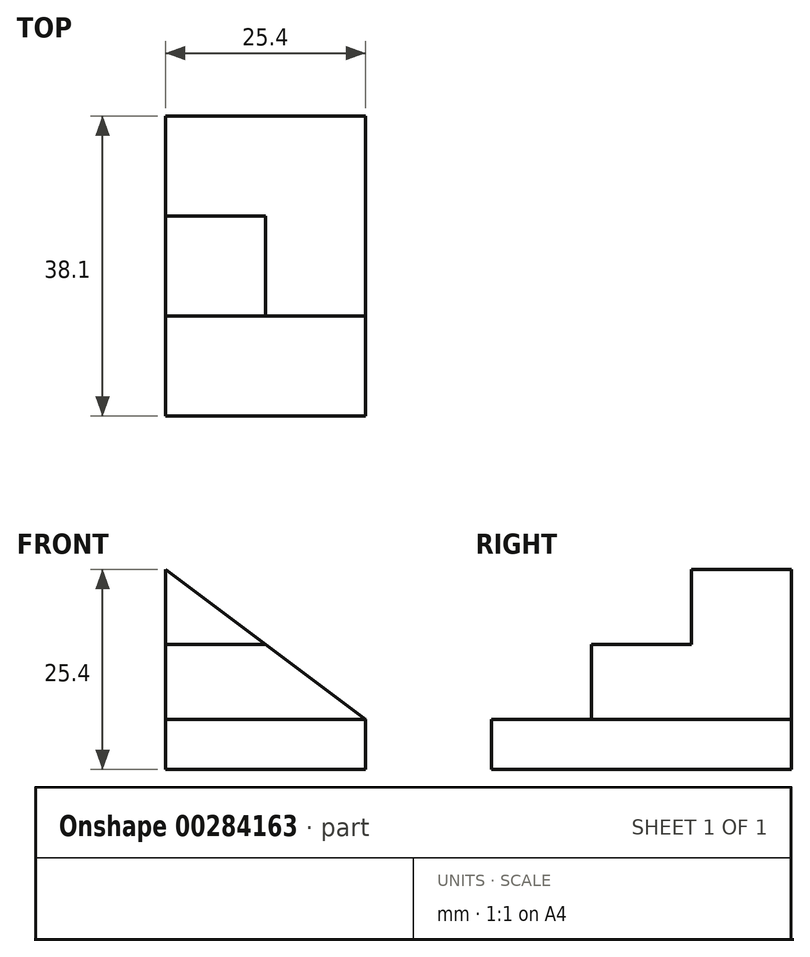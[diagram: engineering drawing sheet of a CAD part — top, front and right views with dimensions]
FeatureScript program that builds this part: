
annotation { "Feature Type Name" : "Feature", "Feature Type Description" : "" }
export const myFeature = defineFeature(function(context is Context, id is Id, definition is map)
    precondition{}
    {
        {
            var Q0;
            Q0=qCreatedBy(makeId("Front.planeOp"),FACE);
            var sketch = newSketch(context, id + "F0", { "sketchPlane" : qUnion([Q0])});
            skLineSegment(sketch, "E0.bottom", {"start": v(0, 0) * mm, "end": v(25.4, 0) * mm});
            skLineSegment(sketch, "E0.top", {"start": v(0, 6.35) * mm, "end": v(25.4, 6.35) * mm});
            skLineSegment(sketch, "E0.left", {"start": v(0, 0) * mm, "end": v(0, 6.35) * mm});
            skLineSegment(sketch, "E0.right", {"start": v(25.4, 0) * mm, "end": v(25.4, 6.35) * mm});
            skLineSegment(sketch, "E1.left", {"start": v(0, 6.35) * mm, "end": v(0, 19.05) * mm});
            skLineSegment(sketch, "E1.right", {"start": v(19.05, 6.35) * mm, "end": v(19.05, 11.11) * mm});
            skLineSegment(sketch, "E2.left", {"start": v(0, 19.05) * mm, "end": v(0, 25.4) * mm});
            skLineSegment(sketch, "E3", {"start": v(0, 25.4) * mm, "end": v(25.4, 6.35) * mm});
            skLineSegment(sketch, "E4", {"start": v(0, 19.05) * mm, "end": v(8.47, 19.05) * mm});
            skSolve(sketch);
        }
        {
            var Q0;
            Q0 = qSketchRegion(id + "F0", true);
            extrude(context, id + "F1", {"entities" : qUnion([Q0]), "depth" : 38.1 * mm});
        }
        {
            var Q0;
            Q0=makeQuery(id+"F1.opExtrude","CAP_FACE",FACE,{"disambiguationData":[OSD([sQuery(id+"F0.wireOp",EDGE,"E0.bottom"),sQuery(id+"F0.wireOp",EDGE,"E0.left"),sQuery(id+"F0.wireOp",EDGE,"E0.right"),sQuery(id+"F0.wireOp",EDGE,"E1.left"),sQuery(id+"F0.wireOp",EDGE,"E2.left"),sQuery(id+"F0.wireOp",EDGE,"E3")])],"isStart":false});
            var sketch = newSketch(context, id + "F2", { "sketchPlane" : qUnion([Q0])});
            skLineSegment(sketch, "E5", {"start": v(25.4, 6.35) * mm, "end": v(0, 6.35) * mm});
            skSolve(sketch);
        }
        {
            var Q0;
            {var subQ0=sQuery(id+"F2.wireOp",EDGE,"E5");Q0=makeQuery(id+"F2.imprint","IMPRINT",FACE,{"disambiguationData":[TD([[makeQuery(id+"F2.imprint","IMPRINT",EDGE,{"derivedFrom":subQ0}),-1.0]])]});}
            extrude(context, id + "F3", {"entities" : qUnion([Q0]), "operationType" : NewBodyOperationType.REMOVE, "oppositeDirection" : true, "depth" : 12.7 * mm});
        }
        {
            var Q0;
            Q0=makeQuery(id+"F3.boolean.opBoolean","COPY",FACE,{"derivedFrom":makeQuery(id+"F3.opExtrude","CAP_FACE",FACE,{"disambiguationData":[OSD([sQuery(id+"F0.wireOp",EDGE,"E0.left"),sQuery(id+"F0.wireOp",EDGE,"E1.left"),sQuery(id+"F0.wireOp",EDGE,"E2.left"),sQuery(id+"F0.wireOp",EDGE,"E3"),sQuery(id+"F2.wireOp",EDGE,"E5")])],"isStart":false})});
            var sketch = newSketch(context, id + "F4", { "sketchPlane" : qUnion([Q0])});
            skLineSegment(sketch, "E6", {"start": v(12.7, 15.88) * mm, "end": v(0, 15.88) * mm});
            skSolve(sketch);
        }
        {
            var Q0;
            {var subQ0=sQuery(id+"F4.wireOp",EDGE,"E6");Q0=makeQuery(id+"F4.imprint","IMPRINT",FACE,{"disambiguationData":[TD([[makeQuery(id+"F4.imprint","IMPRINT",EDGE,{"derivedFrom":subQ0}),-1.0]])]});}
            extrude(context, id + "F5", {"entities" : qUnion([Q0]), "operationType" : NewBodyOperationType.REMOVE, "oppositeDirection" : true, "depth" : 12.7 * mm});
        }
    });
